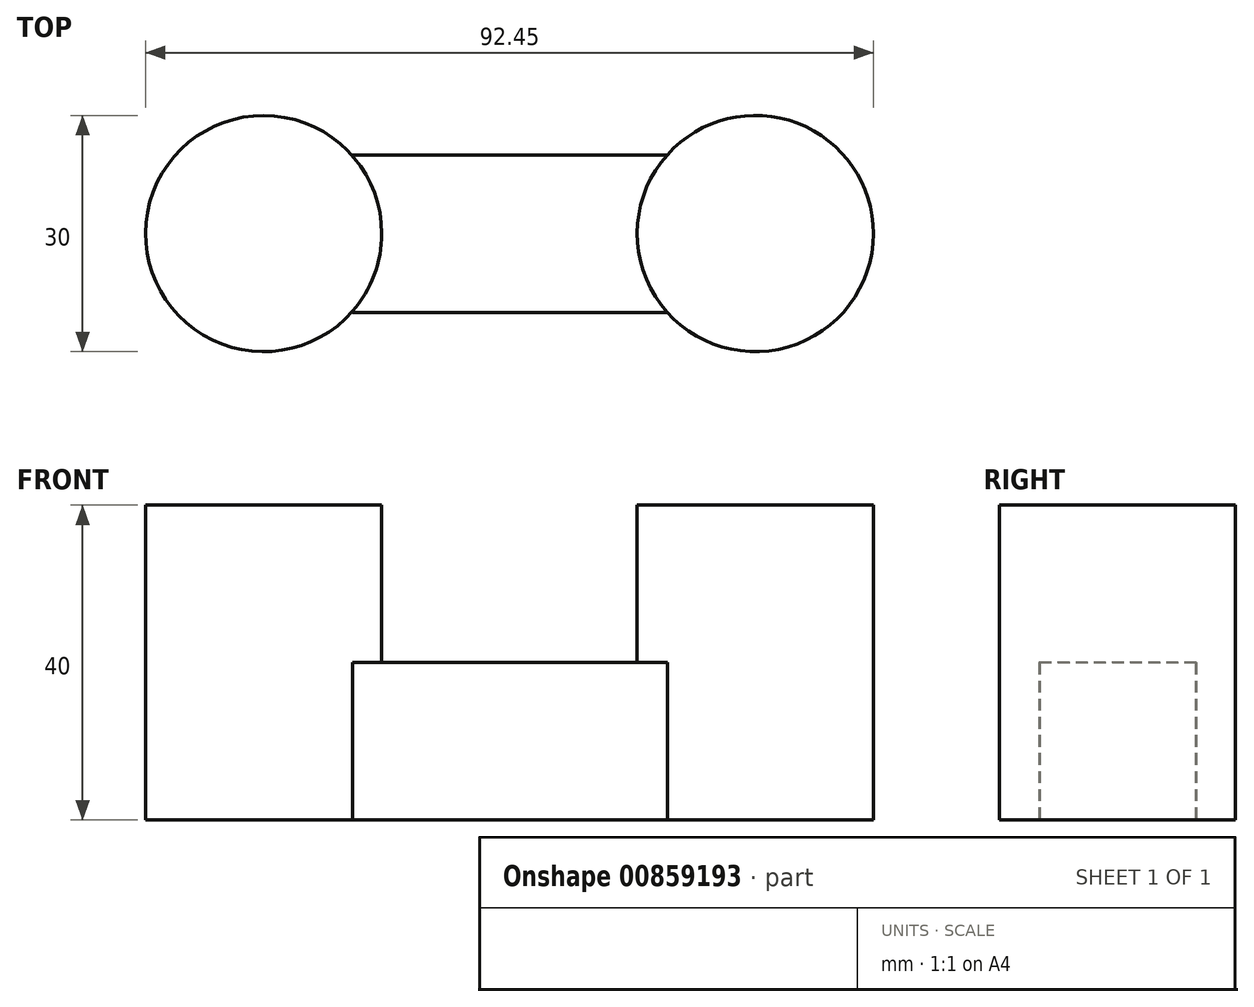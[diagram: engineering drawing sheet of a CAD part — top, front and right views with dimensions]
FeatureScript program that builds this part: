
annotation { "Feature Type Name" : "Feature", "Feature Type Description" : "" }
export const myFeature = defineFeature(function(context is Context, id is Id, definition is map)
    precondition{}
    {
        {
            var Q0;
            Q0=qCreatedBy(makeId("Top.planeOp"),FACE);
            var sketch = newSketch(context, id + "F0", { "sketchPlane" : qUnion([Q0])});
            skLineSegment(sketch, "E0.bottom", {"start": v(20, 10) * mm, "end": v(-20, 10) * mm});
            skLineSegment(sketch, "E0.top", {"start": v(20, -10) * mm, "end": v(-20, -10) * mm});
            skLineSegment(sketch, "E0.left", {"start": v(20, 10) * mm, "end": v(20, -10) * mm});
            skLineSegment(sketch, "E0.right", {"start": v(-20, 10) * mm, "end": v(-20, -10) * mm});
            skPoint(sketch, "E0.middle", {"position": v(0, 0) * mm});
            skSolve(sketch);
        }
        {
            var Q0;
            Q0=qCreatedBy(makeId("Top.planeOp"),FACE);
            var sketch = newSketch(context, id + "F1", { "sketchPlane" : qUnion([Q0])});
            skCircle(sketch, "E1", {"center": v(-31.3, 0) * mm, "radius": 15 * mm});
            skCircle(sketch, "E2", {"center": v(31.16, 0) * mm, "radius": 15 * mm});
            skSolve(sketch);
        }
        {
            var Q0;
            Q0=makeQuery(id+"F0.imprint","IMPRINT",FACE,{"disambiguationData":[TD([[makeQuery(id+"F0.imprint","IMPRINT",EDGE,{"derivedFrom":sQuery(id+"F0.wireOp",EDGE,"E0.bottom")}),1.0]])]});
            extrude(context, id + "F2", {"entities" : qUnion([Q0]), "depth" : 20 * mm, "offsetDistance" : 25 * mm});
        }
        {
            var Q0;
            Q0=makeQuery(id+"F1.imprint","IMPRINT",FACE,{"disambiguationData":[TD([[makeQuery(id+"F1.imprint","IMPRINT",EDGE,{"derivedFrom":sQuery(id+"F1.wireOp",EDGE,"E1")}),1.0]])]});
            var Q1;
            Q1=makeQuery(id+"F1.imprint","IMPRINT",FACE,{"disambiguationData":[TD([[makeQuery(id+"F1.imprint","IMPRINT",EDGE,{"derivedFrom":sQuery(id+"F1.wireOp",EDGE,"E2")}),1.0]])]});
            extrude(context, id + "F3", {"entities" : qUnion([Q0, Q1]), "operationType" : NewBodyOperationType.ADD, "depth" : 40 * mm, "offsetDistance" : 25 * mm});
        }
    });
